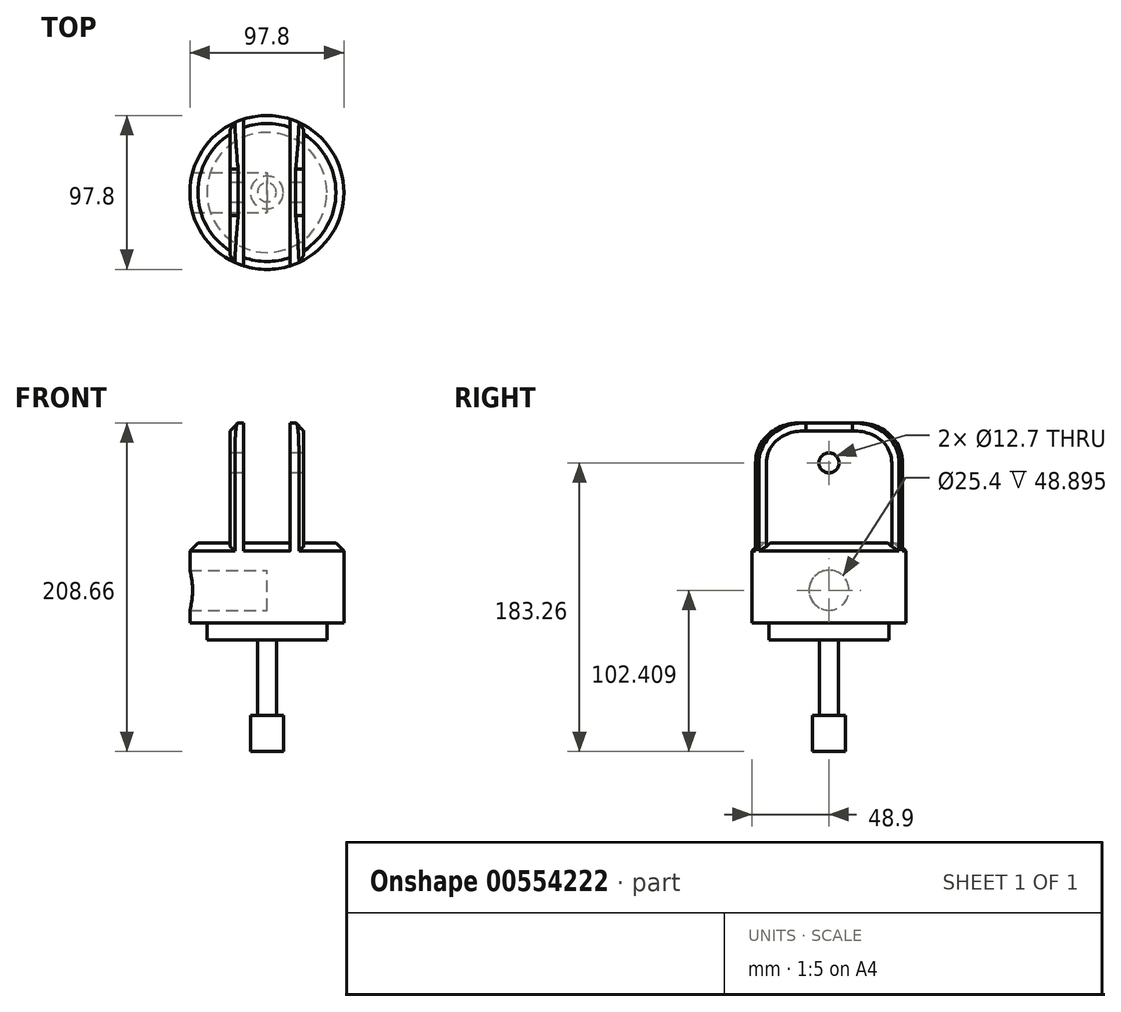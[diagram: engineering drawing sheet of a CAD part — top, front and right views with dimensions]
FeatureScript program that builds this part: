
annotation { "Feature Type Name" : "Feature", "Feature Type Description" : "" }
export const myFeature = defineFeature(function(context is Context, id is Id, definition is map)
    precondition{}
    {
        {
            var Q0;
            Q0=qCreatedBy(makeId("Top.planeOp"),FACE);
            var sketch = newSketch(context, id + "F0", { "sketchPlane" : qUnion([Q0])});
            skCircle(sketch, "E0", {"center": v(0, 0) * mm, "radius": 48.9 * mm});
            skCircle(sketch, "E1", {"center": v(0, 0) * mm, "radius": 38.1 * mm});
            skCircle(sketch, "E2", {"center": v(0, 0) * mm, "radius": 5.97 * mm});
            skSolve(sketch);
        }
        {
            var Q0;
            Q0=makeQuery(id+"F0.imprint","IMPRINT",FACE,{"disambiguationData":[TD([[makeQuery(id+"F0.imprint","IMPRINT",EDGE,{"derivedFrom":sQuery(id+"F0.wireOp",EDGE,"E1")}),1.0]])]});
            var Q1;
            Q1=makeQuery(id+"F0.imprint","IMPRINT",FACE,{"disambiguationData":[TD([[makeQuery(id+"F0.imprint","IMPRINT",EDGE,{"derivedFrom":sQuery(id+"F0.wireOp",EDGE,"E2")}),1.0]])]});
            extrude(context, id + "F1", {"entities" : qUnion([Q0, Q1]), "oppositeDirection" : true, "depth" : 10.8 * mm, "offsetDistance" : 25.4 * mm});
        }
        {
            var Q0;
            Q0=makeQuery(id+"F1.opExtrude","CAP_FACE",FACE,{"disambiguationData":[OSD([sQuery(id+"F0.wireOp",EDGE,"E1")])],"isStart":true});
            var sketch = newSketch(context, id + "F2", { "sketchPlane" : qUnion([Q0])});
            skCircle(sketch, "E3", {"center": v(0, 0) * mm, "radius": 48.9 * mm});
            skSolve(sketch);
        }
        {
            var Q0;
            Q0 = qSketchRegion(id + "F2", true);
            extrude(context, id + "F3", {"entities" : qUnion([Q0]), "operationType" : NewBodyOperationType.ADD, "depth" : 50.8 * mm, "offsetDistance" : 25.4 * mm});
        }
        {
            var Q0;
            Q0=makeQuery(id+"F1.opExtrude","CAP_FACE",FACE,{"disambiguationData":[OSD([sQuery(id+"F0.wireOp",EDGE,"E1")])],"isStart":false});
            var sketch = newSketch(context, id + "F4", { "sketchPlane" : qUnion([Q0])});
            skCircle(sketch, "E4", {"center": v(0, 0) * mm, "radius": 5.97 * mm});
            skSolve(sketch);
        }
        {
            var Q0;
            Q0 = qSketchRegion(id + "F4", true);
            extrude(context, id + "F5", {"entities" : qUnion([Q0]), "operationType" : NewBodyOperationType.ADD, "depth" : 70.87 * mm, "offsetDistance" : 25.4 * mm});
        }
        {
            var Q0;
            Q0=makeQuery(id+"F5.opExtrude","CAP_FACE",FACE,{"disambiguationData":[OSD([sQuery(id+"F4.wireOp",EDGE,"E4")])],"isStart":false});
            var sketch = newSketch(context, id + "F6", { "sketchPlane" : qUnion([Q0])});
            skCircle(sketch, "E5", {"center": v(0, 0) * mm, "radius": 10.44 * mm});
            skSolve(sketch);
        }
        {
            var Q0;
            Q0=makeQuery(id+"F6.imprint","IMPRINT",FACE,{"disambiguationData":[TD([[makeQuery(id+"F6.imprint","IMPRINT",EDGE,{"derivedFrom":sQuery(id+"F6.wireOp",EDGE,"E5")}),1.0]])]});
            extrude(context, id + "F7", {"entities" : qUnion([Q0]), "operationType" : NewBodyOperationType.ADD, "oppositeDirection" : true, "depth" : 22.86 * mm, "offsetDistance" : 25.4 * mm});
        }
        {
            var Q0;
            Q0=makeQuery(id+"F3.opExtrude","CAP_FACE",FACE,{"disambiguationData":[OSD([sQuery(id+"F2.wireOp",EDGE,"E3")])],"isStart":false});
            var sketch = newSketch(context, id + "F8", { "sketchPlane" : qUnion([Q0])});
            skLineSegment(sketch, "E6", {"start": v(0, 0) * mm, "end": v(19.05, 0) * mm});
            skLineSegment(sketch, "E7.bottom", {"start": v(23.33, 46.6) * mm, "end": v(14.77, 46.6) * mm});
            skLineSegment(sketch, "E7.top", {"start": v(23.33, -46.6) * mm, "end": v(14.77, -46.6) * mm});
            skLineSegment(sketch, "E7.left", {"start": v(23.33, 46.6) * mm, "end": v(23.33, -46.6) * mm});
            skLineSegment(sketch, "E7.right", {"start": v(14.77, 46.6) * mm, "end": v(14.77, -46.6) * mm});
            skPoint(sketch, "E7.middle", {"position": v(19.05, 0) * mm});
            skLineSegment(sketch, "E8", {"start": v(0, 0) * mm, "end": v(-19.05, 0) * mm});
            skLineSegment(sketch, "E9.bottom", {"start": v(-23.33, 46.6) * mm, "end": v(-14.77, 46.6) * mm});
            skLineSegment(sketch, "E9.top", {"start": v(-23.33, -46.6) * mm, "end": v(-14.77, -46.6) * mm});
            skLineSegment(sketch, "E9.left", {"start": v(-23.33, 46.6) * mm, "end": v(-23.33, -46.6) * mm});
            skLineSegment(sketch, "E9.right", {"start": v(-14.77, 46.6) * mm, "end": v(-14.77, -46.6) * mm});
            skPoint(sketch, "E9.middle", {"position": v(-19.05, 0) * mm});
            skSolve(sketch);
        }
        {
            var Q0;
            {var subQ0=sQuery(id+"F8.wireOp",EDGE,"E9.right");var subQ1=sQuery(id+"F8.wireOp",EDGE,"E9.bottom");var subQ2=makeQuery(id+"F8.imprint","INTERSECT",VERTEX,{"derivedFrom":[subQ1,subQ0]});Q0=makeQuery(id+"F8.imprint","IMPRINT",FACE,{"disambiguationData":[TD([[makeQuery(id+"F8.imprint","IMPRINT",EDGE,{"disambiguationData":[TD([[subQ2,1.0]])],"derivedFrom":subQ1}),-1.0]])]});}
            var Q1;
            {var subQ0=sQuery(id+"F8.wireOp",EDGE,"E7.right");var subQ1=sQuery(id+"F8.wireOp",EDGE,"E7.bottom");var subQ2=makeQuery(id+"F8.imprint","INTERSECT",VERTEX,{"derivedFrom":[subQ1,subQ0]});Q1=makeQuery(id+"F8.imprint","IMPRINT",FACE,{"disambiguationData":[TD([[makeQuery(id+"F8.imprint","IMPRINT",EDGE,{"disambiguationData":[TD([[subQ2,1.0]])],"derivedFrom":subQ1}),1.0]])]});}
            extrude(context, id + "F9", {"entities" : qUnion([Q0, Q1]), "operationType" : NewBodyOperationType.ADD, "depth" : 76.2 * mm, "offsetDistance" : 25.4 * mm});
        }
        {
            var Q0;
            {var subQ0=sQuery(id+"F2.wireOp",EDGE,"E3");var subQ1=makeQuery(id+"F3.opExtrude","CAP_EDGE",EDGE,{"disambiguationData":[OSD([subQ0])],"isStart":false});Q0=makeQuery(id+"F9.opExtrude","CAP_EDGE",EDGE,{"disambiguationData":[OSD([subQ0]),TDD([makeQuery(id+"F8.imprint","IMPRINT",EDGE,{"disambiguationData":[TD([[makeQuery(id+"F8.imprint","INTERSECT",VERTEX,{"derivedFrom":[subQ1,sQuery(id+"F8.wireOp",EDGE,"E9.top")]}),1.0]])],"derivedFrom":subQ1})])],"isStart":false});}
            var Q1;
            {var subQ0=sQuery(id+"F2.wireOp",EDGE,"E3");var subQ1=makeQuery(id+"F3.opExtrude","CAP_EDGE",EDGE,{"disambiguationData":[OSD([subQ0])],"isStart":false});Q1=makeQuery(id+"F9.opExtrude","CAP_EDGE",EDGE,{"disambiguationData":[OSD([subQ0]),TDD([makeQuery(id+"F8.imprint","IMPRINT",EDGE,{"disambiguationData":[TD([[makeQuery(id+"F8.imprint","INTERSECT",VERTEX,{"derivedFrom":[subQ1,sQuery(id+"F8.wireOp",EDGE,"E9.bottom")]}),-1.0]])],"derivedFrom":subQ1})])],"isStart":false});}
            var Q2;
            {var subQ0=sQuery(id+"F2.wireOp",EDGE,"E3");var subQ1=makeQuery(id+"F3.opExtrude","CAP_EDGE",EDGE,{"disambiguationData":[OSD([subQ0])],"isStart":false});Q2=makeQuery(id+"F9.opExtrude","CAP_EDGE",EDGE,{"disambiguationData":[OSD([subQ0]),TDD([makeQuery(id+"F8.imprint","IMPRINT",EDGE,{"disambiguationData":[TD([[makeQuery(id+"F8.imprint","INTERSECT",VERTEX,{"derivedFrom":[subQ1,sQuery(id+"F8.wireOp",EDGE,"E7.top")]}),-1.0]])],"derivedFrom":subQ1})])],"isStart":false});}
            var Q3;
            {var subQ0=sQuery(id+"F2.wireOp",EDGE,"E3");var subQ1=makeQuery(id+"F3.opExtrude","CAP_EDGE",EDGE,{"disambiguationData":[OSD([subQ0])],"isStart":false});Q3=makeQuery(id+"F9.opExtrude","CAP_EDGE",EDGE,{"disambiguationData":[OSD([subQ0]),TDD([makeQuery(id+"F8.imprint","IMPRINT",EDGE,{"disambiguationData":[TD([[makeQuery(id+"F8.imprint","INTERSECT",VERTEX,{"derivedFrom":[subQ1,sQuery(id+"F8.wireOp",EDGE,"E7.bottom")]}),1.0]])],"derivedFrom":subQ1})])],"isStart":false});}
            fillet(context, id + "F10", {"entities" : qUnion([Q0, Q1, Q2, Q3]), "radius" : 25.4 * mm, "tangentPropagation" : true, "allowEdgeOverflow" : false});
        }
        {
            var Q0;
            Q0=makeQuery(id+"F9.opExtrude","SWEPT_FACE",FACE,{"disambiguationData":[OSD([sQuery(id+"F8.wireOp",EDGE,"E9.left")])]});
            var sketch = newSketch(context, id + "F11", { "sketchPlane" : qUnion([Q0])});
            skLineSegment(sketch, "E10", {"start": v(0, 50.8) * mm, "end": v(0, 101.6) * mm});
            skPoint(sketch, "E10.endSnap0", {"position": v(0, 50.8) * mm});
            skCircle(sketch, "E11", {"center": v(0, 101.6) * mm, "radius": 6.35 * mm});
            skSolve(sketch);
        }
        {
            var Q0;
            Q0 = qSketchRegion(id + "F11", true);
            extrude(context, id + "F12", {"entities" : qUnion([Q0]), "operationType" : NewBodyOperationType.REMOVE, "oppositeDirection" : true, "depth" : 97.54 * mm, "offsetDistance" : 25.4 * mm});
        }
        {
            var Q0;
            Q0=makeQuery(id+"F1.opExtrude","SWEPT_BODY",BODY,{"disambiguationData":[OSD([sQuery(id+"F0.wireOp",EDGE,"E1")])]});
            transform(context, id + "F13", {"entities" : qUnion([Q0]), "transformType" : TransformType.TRANSLATION_3D, "dx" : 0 * mm, "dy" : 0 * mm, "dz" : 0 * mm, "makeCopy" : true});
        }
        {
            var Q0;
            Q0=makeQuery(id+"F13.opPattern","COPY",BODY,{"derivedFrom":makeQuery(id+"F1.opExtrude","SWEPT_BODY",BODY,{"disambiguationData":[OSD([sQuery(id+"F0.wireOp",EDGE,"E1")])]}),"instanceName":"1"});
            deleteBodies(context, id + "F14", {"entities" : qUnion([Q0])});
        }
        {
            var Q0;
            {var subQ1=sQuery(id+"F2.wireOp",EDGE,"E3");var subQ2=sQuery(id+"F8.wireOp",EDGE,"E7.top");var subQ3=makeQuery(id+"F3.opExtrude","CAP_EDGE",EDGE,{"disambiguationData":[OSD([subQ1])],"isStart":false});Q0=makeQuery(id+"F9.boolean.opBoolean","SPLIT",EDGE,{"disambiguationData":[TD([makeQuery(id+"F9.opExtrude","SWEPT_FACE",FACE,{"disambiguationData":[OSD([subQ2])]})])],"derivedFrom":subQ3});}
            var Q1;
            {var subQ0=sQuery(id+"F2.wireOp",EDGE,"E3");var subQ1=makeQuery(id+"F3.opExtrude","CAP_EDGE",EDGE,{"disambiguationData":[OSD([subQ0])],"isStart":false});var subQ3=sQuery(id+"F8.wireOp",EDGE,"E9.left");Q1=makeQuery(id+"F9.boolean.opBoolean","SPLIT",EDGE,{"disambiguationData":[TD([makeQuery(id+"F9.opExtrude","SWEPT_FACE",FACE,{"disambiguationData":[OSD([subQ3])]})])],"derivedFrom":subQ1});}
            var Q2;
            {var subQ0=sQuery(id+"F2.wireOp",EDGE,"E3");var subQ1=makeQuery(id+"F3.opExtrude","CAP_EDGE",EDGE,{"disambiguationData":[OSD([subQ0])],"isStart":false});var subQ2=sQuery(id+"F8.wireOp",EDGE,"E7.left");Q2=makeQuery(id+"F9.boolean.opBoolean","SPLIT",EDGE,{"disambiguationData":[TD([makeQuery(id+"F9.opExtrude","SWEPT_FACE",FACE,{"disambiguationData":[OSD([subQ2])]})])],"derivedFrom":subQ1});}
            var Q3;
            {var subQ1=sQuery(id+"F8.wireOp",EDGE,"E7.bottom");var subQ2=sQuery(id+"F2.wireOp",EDGE,"E3");var subQ3=makeQuery(id+"F3.opExtrude","CAP_EDGE",EDGE,{"disambiguationData":[OSD([subQ2])],"isStart":false});Q3=makeQuery(id+"F9.boolean.opBoolean","SPLIT",EDGE,{"disambiguationData":[TD([makeQuery(id+"F9.opExtrude","SWEPT_FACE",FACE,{"disambiguationData":[OSD([subQ1])]})])],"derivedFrom":subQ3});}
            var Q4;
            {var subQ0=sQuery(id+"F8.wireOp",EDGE,"E9.left");var subQ1=sQuery(id+"F2.wireOp",EDGE,"E3");var subQ2=makeQuery(id+"F3.opExtrude","CAP_EDGE",EDGE,{"disambiguationData":[OSD([subQ1])],"isStart":false});Q4=makeQuery(id+"F10.opFillet","BLEND_EDGE",EDGE,{"blendedFrom":[makeQuery(id+"F9.opExtrude","CAP_EDGE",EDGE,{"disambiguationData":[OSD([subQ1]),TDD([makeQuery(id+"F8.imprint","IMPRINT",EDGE,{"disambiguationData":[TD([[makeQuery(id+"F8.imprint","INTERSECT",VERTEX,{"derivedFrom":[subQ2,sQuery(id+"F8.wireOp",EDGE,"E9.top")]}),1.0]])],"derivedFrom":subQ2})])],"isStart":false}),makeQuery(id+"F9.opExtrude","SWEPT_FACE",FACE,{"disambiguationData":[OSD([subQ0])]})],"blendedInto":[makeQuery(id+"F9.opExtrude","SWEPT_FACE",FACE,{"disambiguationData":[OSD([subQ0])]})]});}
            var Q5;
            {var subQ0=sQuery(id+"F8.wireOp",EDGE,"E7.left");var subQ1=sQuery(id+"F2.wireOp",EDGE,"E3");Q5=makeQuery(id+"F9.opExtrude","SWEPT_EDGE",EDGE,{"disambiguationData":[OSD([subQ1,subQ0]),TDD([makeQuery(id+"F8.imprint","INTERSECT",VERTEX,{"disambiguationData":[OD(1.0)],"derivedFrom":[makeQuery(id+"F3.opExtrude","CAP_EDGE",EDGE,{"disambiguationData":[OSD([subQ1])],"isStart":false}),subQ0]})])]});}
            chamfer(context, id + "F15", {"entities" : qUnion([Q0, Q1, Q2, Q3, Q4, Q5]), "width" : 5.08 * mm, "tangentPropagation" : true});
        }
        {
            var Q0;
            Q0=qCreatedBy(makeId("Right.planeOp"),FACE);
            var sketch = newSketch(context, id + "F16", { "sketchPlane" : qUnion([Q0])});
            skCircle(sketch, "E12", {"center": v(0, 20.75) * mm, "radius": 12.7 * mm});
            skSolve(sketch);
        }
        {
            var Q0;
            Q0 = qSketchRegion(id + "F16", true);
            extrude(context, id + "F17", {"entities" : qUnion([Q0]), "operationType" : NewBodyOperationType.REMOVE, "oppositeDirection" : true, "depth" : 107.7 * mm, "offsetDistance" : 25.4 * mm});
        }
    });
